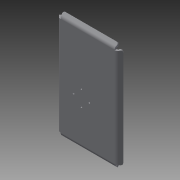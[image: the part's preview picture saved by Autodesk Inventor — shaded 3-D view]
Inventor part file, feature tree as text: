
AUTODESK INVENTOR PART (.ipt)
format: ipt  version: 2013 (Build 170138000, 138)  size: 135,680 bytes
history: native  units: in
note: dims shown in document units (in); Inventor stores cm internally (conversion verified against a paired STEP export)
features: reference x7, sheet_metal_op x4, sketch x2, other x2, chamfer x1
ambient origin geometry x8: Origin, YZ Plane, XZ Plane, XY Plane, X Axis, Y Axis, Z Axis, Center Point
bodies: Solid1 (feature_tree)
feature tree (16):
  sheet_metal_op  "Face1"
  sheet_metal_op  "Flange1"
  chamfer  "Corner Round1"
  sketch  "Sketch1"  dims[d0=2.1654in]
  reference  "Reference1"
  reference  "Reference2"
  reference  "Reference3"
  reference  "Reference4"
  reference  "Reference5"
  reference  "Reference6"
  reference  "Reference7"
  other  "Plate1"
  sketch  "Sketch2"  dims[d1=3.937in d2=0.0787in d3=0.0787in d4=0.0394in d5=0.1575in d6=0.0787in d7=0.1969in d8=45.0deg d9=0.0787in d10=0.315in d11=0.0787in d12=0.0787in d13=0.0787in]
  other  "Plate2"
  sheet_metal_op  "Bend1"
  sheet_metal_op  "Corner1"
